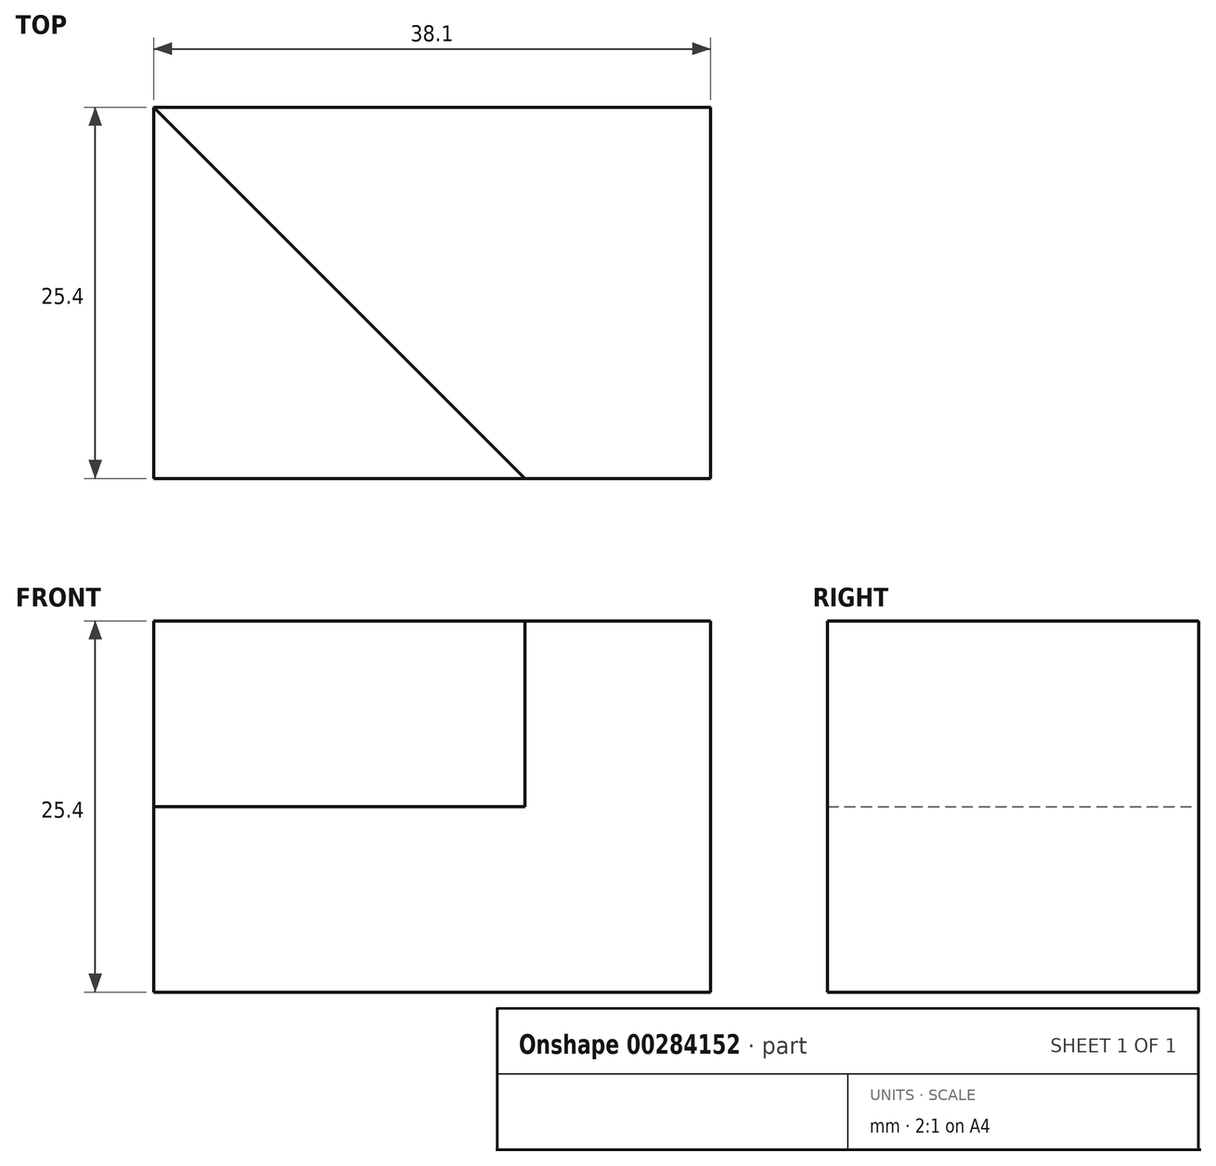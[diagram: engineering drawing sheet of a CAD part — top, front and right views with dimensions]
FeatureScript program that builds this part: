
annotation { "Feature Type Name" : "Feature", "Feature Type Description" : "" }
export const myFeature = defineFeature(function(context is Context, id is Id, definition is map)
    precondition{}
    {
        {
            var Q0;
            Q0=qCreatedBy(makeId("Top.planeOp"),FACE);
            var sketch = newSketch(context, id + "F0", { "sketchPlane" : qUnion([Q0])});
            skLineSegment(sketch, "E0.bottom", {"start": v(0, 0) * mm, "end": v(38.1, 0) * mm});
            skLineSegment(sketch, "E0.top", {"start": v(0, 25.4) * mm, "end": v(38.1, 25.4) * mm});
            skLineSegment(sketch, "E0.left", {"start": v(0, 0) * mm, "end": v(0, 25.4) * mm});
            skLineSegment(sketch, "E0.right", {"start": v(38.1, 0) * mm, "end": v(38.1, 25.4) * mm});
            skLineSegment(sketch, "E1", {"start": v(25.4, 0) * mm, "end": v(0, 0) * mm});
            skLineSegment(sketch, "E2", {"start": v(0, 25.4) * mm, "end": v(25.4, 0) * mm});
            skLineSegment(sketch, "E3", {"start": v(38.1, 25.4) * mm, "end": v(19.05, 25.4) * mm});
            skLineSegment(sketch, "E4", {"start": v(19.05, 25.4) * mm, "end": v(38.1, 6.35) * mm});
            skSolve(sketch);
        }
        {
            var Q0;
            Q0 = qSketchRegion(id + "F0", true);
            extrude(context, id + "F1", {"entities" : qUnion([Q0]), "oppositeDirection" : true, "depth" : 25.4 * mm});
        }
        {
            var Q0;
            {var subQ1=sQuery(id+"F0.wireOp",EDGE,"E0.bottom");Q0=makeQuery(id+"F0.imprint","IMPRINT",FACE,{"disambiguationData":[TD([[makeQuery(id+"F0.imprint","IMPRINT",EDGE,{"derivedFrom":subQ1}),1.0]])]});}
            extrude(context, id + "F2", {"entities" : qUnion([Q0]), "operationType" : NewBodyOperationType.REMOVE, "oppositeDirection" : true, "depth" : 12.7 * mm});
        }
    });
